# Revit family: LPKB Silent 200 C1 EC_7540664
name_source: partatom
category: Mechanical Equipment
revit_build: Autodesk Revit MEP 2014 (Build: 20130308_1515(x64)
units: mm (PartAtom-declared; Revit-internal decimal feet)

## types (1)
- LPKB Silent 200 C1 EC
    Capacitor = -
    Current = 1 A
    Depth = 390 mm  [stored 1.27953 ft]
    Description = SOUND ATTENUATED DUCT FANS WITH CIRCULAR CONNECTIONS
    Diameter = 200 mm  [stored 0.656168 ft]
    Distance 1 = 111 mm  [stored 0.364173 ft]
    Distance 2 = 220 mm
    Frequency = 50 Hz
    Height = 288 mm  [stored 0.944882 ft]
    Main Material = Steel, Galvanized
    Max. temperature of transported air = 60 °C
    Max. temperature of transported air when speed controlled = 60 °C
    Phase = 1
    Power = 162 W
    Radius = 100 mm  [stored 0.328084 ft]
    Sound pressure level at 3 m = 57
    Speed = 2820
    Vertical Distance = 162 mm
    Voltage = 230 V
    Voltage range = 200-240
    Weight = 8.30 kg
    Width = 468 mm  [stored 1.53543 ft]
    Width A = 372 mm  [stored 1.22047 ft]
    Wiring diagram = 4040143

note: [stored X ft] marks values corroborated as IEEE doubles in the binary element streams (Revit-internal decimal feet)

## geometry (parser evidence)
native form markers: Sweep x6
no freeform markers — native parametric forms only
